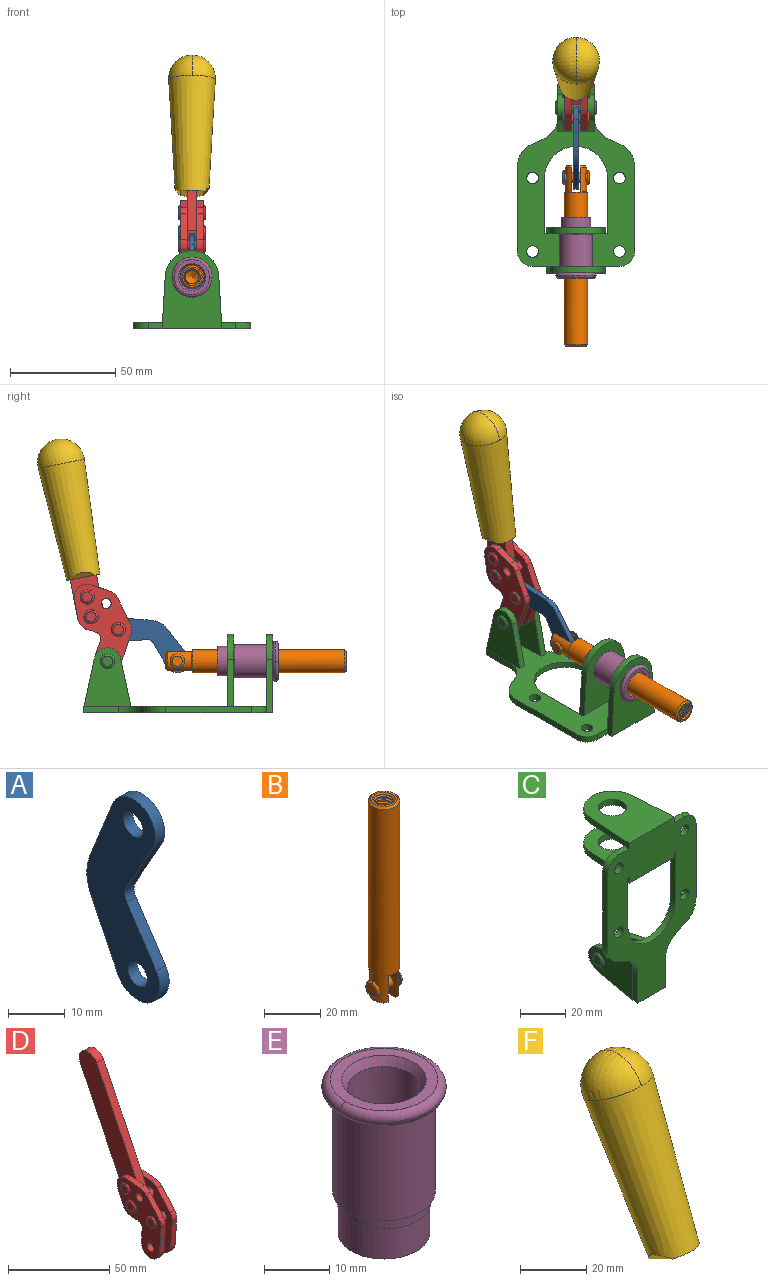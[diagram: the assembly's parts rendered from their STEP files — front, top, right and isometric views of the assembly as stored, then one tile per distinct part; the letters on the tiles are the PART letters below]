
ASSEMBLY  parts=6 mates=6
PART A: 12 faces, bbox 2.3x18.2x42.8 mm
  f0: cylinder r=2.4mm len=4.8mm, axis (1,0,0), area 34.9mm2, adj f4,f11
  f1: cylinder r=10.41mm len=8.47mm, axis (1,0,0), area 20.2mm2, adj f4,f9,f10,f11
  f2: cylinder r=3.05mm len=3.16mm, axis (1,0,0), area 7.7mm2, adj f4,f6,f7,f11
  f3: cylinder r=2.4mm len=4.8mm, axis (1,0,0), area 34.9mm2, adj f4,f11
  f4: plane 42.81x18.23mm, normal (-1,0,0), area 414.1mm2, adj f0,f1,f2,f3,f5,f6,f7,f8
  f5: cylinder r=5.54mm len=10.67mm, axis (1,0,0), area 41.8mm2, adj f4,f6,f10,f11
  f6: plane 11.66x6.53mm, normal (0,-0.87,-0.49), area 30.9mm2, adj f2,f4,f5,f11
  f7: plane 11.17x7.33mm, normal (0,-0.84,0.55), area 30.9mm2, adj f2,f4,f8,f11
  f8: cylinder r=5.54mm len=10.51mm, axis (1,0,0), area 41.8mm2, adj f4,f7,f9,f11
  f9: plane 13.67x6.67mm, normal (0,0.9,-0.44), area 35.1mm2, adj f1,f4,f8,f11
  f10: plane 14.1x5.7mm, normal (0,0.93,0.37), area 35.1mm2, adj f1,f4,f5,f11
  f11: plane 42.81x18.23mm, normal (1,0,0), area 414.1mm2, adj f0,f1,f2,f3,f5,f6,f7,f8
PART B: 48 faces, bbox 12.6x11.1x86.1 mm
  f0: torus R=2.41mm, axis (-1,0,0), area 15mm2, adj f30,f32,f34
  f1: torus R=2.41mm, axis (-1,0,0), area 15mm2, adj f29,f31,f33
  f2: cylinder r=5.54mm len=72.39mm, axis (0,0,1), area 2518.5mm2, adj f3,f4,f42,f43
  f3: cone r=5.54mm half-angle=45deg, axis (0,0,1), area 7.6mm2, adj f2,f5,f41
  f4: cone r=5.54mm half-angle=45deg, axis (0,0,-1), area 34.9mm2, adj f2,f39
  f5: cylinder r=5.08mm len=11.48mm, axis (0,0,1), area 108.3mm2, adj f3,f7,f8,f41
  f6: cylinder r=2.41mm len=4.83mm, axis (-1,0,0), area 71.2mm2, adj f40,f41
  f7: cylinder r=2.41mm len=4.83mm, axis (-1,0,0), area 7.6mm2, adj f5,f34
  f8: cone r=5.08mm half-angle=45deg, axis (0,0,1), area 10.6mm2, adj f5,f37,f41
  f9: cone r=3.98mm half-angle=45deg, axis (0,0,1), area 17.6mm2, adj f27,f39,f45,f46,f47
  f10: cylinder r=2.41mm len=4.83mm, axis (-1,0,0), area 7.6mm2, adj f33,f38
  f11: cylinder r=3.2mm len=6.4mm, axis (0,0,1), area 78.4mm2, adj f12,f28,f44,f45,f47
  f12: cylinder r=3.2mm len=6.4mm, axis (0,0,1), area 10.5mm2, adj f11,f13,f45,f47
  f13: cylinder r=3.2mm len=6.4mm, axis (0,0,1), area 10.5mm2, adj f12,f14,f45,f47
  f14: cylinder r=3.2mm len=6.4mm, axis (0,0,1), area 10.5mm2, adj f13,f15,f45,f47
  f15: cylinder r=3.2mm len=6.4mm, axis (0,0,1), area 10.5mm2, adj f14,f16,f45,f47
  f16: cylinder r=3.2mm len=6.4mm, axis (0,0,1), area 10.5mm2, adj f15,f17,f45,f47
  f17: cylinder r=3.2mm len=6.4mm, axis (0,0,1), area 10.5mm2, adj f16,f18,f45,f47
  f18: cylinder r=3.2mm len=6.4mm, axis (0,0,1), area 10.5mm2, adj f17,f19,f45,f47
  f19: cylinder r=3.2mm len=6.4mm, axis (0,0,1), area 10.5mm2, adj f18,f20,f45,f47
  f20: cylinder r=3.2mm len=6.4mm, axis (0,0,1), area 10.5mm2, adj f19,f21,f45,f47
  f21: cylinder r=3.2mm len=6.4mm, axis (0,0,1), area 10.5mm2, adj f20,f22,f45,f47
  f22: cylinder r=3.2mm len=6.4mm, axis (0,0,1), area 10.5mm2, adj f21,f23,f45,f47
  f23: cylinder r=3.2mm len=6.4mm, axis (0,0,1), area 10.5mm2, adj f22,f24,f45,f47
  f24: cylinder r=3.2mm len=6.4mm, axis (0,0,1), area 10.5mm2, adj f23,f25,f45,f47
  f25: cylinder r=3.2mm len=6.4mm, axis (0,0,1), area 10.5mm2, adj f24,f26,f45,f47
  f26: cylinder r=3.2mm len=6.4mm, axis (0,0,1), area 10.5mm2, adj f25,f27,f45,f47
  f27: cylinder r=3.2mm len=6.4mm, axis (0,0,1), area 7.4mm2, adj f9,f26,f45,f47
  f28: cone r=3.2mm half-angle=60deg, axis (0,0,1), area 37.2mm2, adj f11
  f29: plane 4.83x4.83mm, normal (-1,0,0), area 18.3mm2, adj f1,f31
  f30: plane 4.83x4.83mm, normal (1,0,0), area 18.3mm2, adj f0,f32
  f31: torus R=2.41mm, axis (-1,0,0), area 15mm2, adj f1,f29,f33
  f32: torus R=2.41mm, axis (-1,0,0), area 15mm2, adj f0,f30,f34
  f33: plane 6.83x6.83mm, normal (1,0,0), area 18.3mm2, adj f1,f10,f31
  f34: plane 6.83x6.83mm, normal (-1,0,0), area 18.3mm2, adj f0,f7,f32
  f35: cone r=5.08mm half-angle=45deg, axis (0,0,1), area 10.6mm2, adj f36,f38,f40
  f36: plane 7.25x1.97mm, normal (0,0,-1), area 10mm2, adj f35,f40
  f37: plane 7.25x1.97mm, normal (0,0,-1), area 10mm2, adj f8,f41
  f38: cylinder r=5.08mm len=11.48mm, axis (0,0,1), area 108.3mm2, adj f10,f35,f40,f42
  f39: plane 9.55x9.55mm, normal (0,0,1), area 22mm2, adj f4,f9
  f40: plane 12.76x10.09mm, normal (1,0,0), area 95.7mm2, adj f6,f35,f36,f38,f42,f43
  f41: plane 12.76x10.09mm, normal (-1,0,0), area 95.7mm2, adj f3,f5,f6,f8,f37,f43
  f42: cone r=5.54mm half-angle=45deg, axis (0,0,1), area 7.6mm2, adj f2,f38,f40
  f43: plane 11.07x4.7mm, normal (0,0,-1), area 50.4mm2, adj f2,f40,f41
  f44: plane 0.89x0.62mm, normal (-1,0,0), area 0.3mm2, adj f11,f45,f46,f47
  f45: bspline ~24.8x7.63mm, area 266.6mm2, adj f9,f11,f12,f13,f14,f15,f16,f17
  f46: bspline ~24.87x7.63mm, area 73.6mm2, adj f9,f44,f45,f47
  f47: bspline ~24.98x7.63mm, area 272.5mm2, adj f9,f11,f12,f13,f14,f15,f16,f17
PART C: 55 faces, bbox 55.7x37.4x89.8 mm
  f0: torus R=2.41mm, axis (-1,0,0), area 15mm2, adj f11,f15,f25
  f1: torus R=2.41mm, axis (-1,0,0), area 15mm2, adj f10,f12,f22
  f2: cylinder r=2.78mm len=5.56mm, axis (0,-1,0), area 54.2mm2, adj f30,f54
  f3: cylinder r=14.99mm len=29.97mm, axis (0,-1,0), area 145.9mm2, adj f30,f49,f53,f54
  f4: cylinder r=2.78mm len=5.56mm, axis (0,-1,0), area 54.2mm2, adj f30,f54
  f5: cylinder r=2.78mm len=5.56mm, axis (0,-1,0), area 54.2mm2, adj f30,f54
  f6: cylinder r=2.78mm len=5.56mm, axis (0,-1,0), area 54.2mm2, adj f30,f54
  f7: cylinder r=6.35mm len=12.7mm, axis (0,0,1), area 123.6mm2, adj f27,f51
  f8: cylinder r=6.35mm len=12.7mm, axis (0,0,-1), area 124.7mm2, adj f21,f35
  f9: cylinder r=2.41mm len=11.18mm, axis (-1,0,0), area 169.4mm2, adj f16,f19
  f10: plane 4.83x4.83mm, normal (1,0,0), area 18.3mm2, adj f1,f12
  f11: plane 4.83x4.83mm, normal (-1,0,0), area 18.3mm2, adj f0,f15
  f12: torus R=2.41mm, axis (-1,0,0), area 15mm2, adj f1,f10,f22
  f13: cylinder r=6.35mm len=12.41mm, axis (1,0,0), area 53.4mm2, adj f18,f19,f22,f23
  f14: cylinder r=6.35mm len=12.41mm, axis (-1,0,0), area 53.4mm2, adj f16,f17,f24,f25
  f15: torus R=2.41mm, axis (-1,0,0), area 15mm2, adj f0,f11,f25
  f16: plane 27.86x22.35mm, normal (1,0,0), area 425.4mm2, adj f9,f14,f17,f24,f30
  f17: plane 22.86x4.97mm, normal (0,0.21,0.98), area 72.5mm2, adj f14,f16,f25,f30
  f18: plane 22.86x4.97mm, normal (0,0.21,0.98), area 72.5mm2, adj f13,f19,f22,f30
  f19: plane 27.86x22.35mm, normal (-1,0,0), area 425.4mm2, adj f9,f13,f18,f23,f30
  f20: cylinder r=12.7mm len=25.35mm, axis (0,0,-1), area 119.8mm2, adj f21,f34,f35,f36
  f21: plane 34.21x28.07mm, normal (0,0,-1), area 702.4mm2, adj f8,f20,f30,f34,f36
  f22: plane 27.96x22.45mm, normal (1,0,0), area 407.2mm2, adj f1,f12,f13,f18,f23,f30,f42,f43
  f23: plane 22.86x4.97mm, normal (0,0.21,-0.98), area 72.5mm2, adj f13,f19,f22,f44
  f24: plane 22.86x4.97mm, normal (0,0.21,-0.98), area 72.5mm2, adj f14,f16,f25,f44
  f25: plane 27.86x22.35mm, normal (-1,0,0), area 407.1mm2, adj f0,f14,f15,f17,f24,f30,f45,f46
  f26: plane 3.1x0.95mm, normal (0,0,-1), area 2.7mm2, adj f30,f49,f50,f54
  f27: plane 34.21x28.07mm, normal (0,0,1), area 702.4mm2, adj f7,f28,f30,f50,f52
  f28: cylinder r=12.7mm len=25.35mm, axis (0,0,1), area 118.8mm2, adj f27,f50,f51,f52
  f29: plane 3.1x0.95mm, normal (0,0,-1), area 2.7mm2, adj f30,f52,f53,f54
  f30: plane 86.54x55.63mm, normal (0,1,0), area 2362.9mm2, adj f2,f3,f4,f5,f6,f16,f17,f18
  f31: plane 40.56x3.1mm, normal (-1,0,0), area 125.7mm2, adj f30,f32,f48,f54
  f32: cylinder r=7.11mm len=7.11mm, axis (0,-1,0), area 34.6mm2, adj f30,f31,f33,f54
  f33: plane 6.67x3.1mm, normal (0,0,1), area 20.4mm2, adj f30,f32,f34,f54
  f34: plane 25.39x3.13mm, normal (-1,0.06,0), area 79.5mm2, adj f20,f21,f33,f35,f54
  f35: plane 37.31x28.45mm, normal (0,0,1), area 789.9mm2, adj f8,f20,f34,f36,f54
  f36: plane 25.39x3.13mm, normal (1,0.06,0), area 79.5mm2, adj f20,f21,f35,f37,f54
  f37: plane 6.67x3.1mm, normal (0,0,1), area 20.4mm2, adj f30,f36,f38,f54
  f38: cylinder r=7.11mm len=7.11mm, axis (0,-1,0), area 34.6mm2, adj f30,f37,f39,f54
  f39: plane 40.56x3.1mm, normal (1,0,0), area 125.7mm2, adj f30,f38,f40,f54
  f40: cylinder r=11.18mm len=10.16mm, axis (0,-1,0), area 39.5mm2, adj f30,f39,f41,f54
  f41: plane 6.09x3.1mm, normal (0.42,0,-0.91), area 20.8mm2, adj f30,f40,f42,f54
  f42: cylinder r=11.18mm len=9.41mm, axis (0,-1,0), area 37.2mm2, adj f22,f30,f41,f43,f54
  f43: plane 16.5x3.1mm, normal (1,0,0), area 51.1mm2, adj f22,f42,f44,f54
  f44: plane 17.37x3.1mm, normal (0,0,-1), area 53.8mm2, adj f23,f24,f30,f43,f45,f54
  f45: plane 16.5x3.1mm, normal (-1,0,0), area 51.1mm2, adj f25,f44,f46,f54
  f46: cylinder r=11.18mm len=9.41mm, axis (0,-1,0), area 37.2mm2, adj f25,f30,f45,f47,f54
  f47: plane 6.09x3.1mm, normal (-0.42,0,-0.91), area 20.8mm2, adj f30,f46,f48,f54
  f48: cylinder r=11.18mm len=10.16mm, axis (0,-1,0), area 39.5mm2, adj f30,f31,f47,f54
  f49: plane 26.54x3.1mm, normal (-1,0,0), area 82.3mm2, adj f3,f26,f30,f54
  f50: plane 25.39x3.1mm, normal (1,0.06,0), area 78.8mm2, adj f26,f27,f28,f51,f54
  f51: plane 37.31x28.45mm, normal (0,0,-1), area 789.9mm2, adj f7,f28,f50,f52,f54
  f52: plane 25.39x3.1mm, normal (-1,0.06,0), area 78.8mm2, adj f27,f28,f29,f51,f54
  f53: plane 26.54x3.1mm, normal (1,0,0), area 82.3mm2, adj f3,f29,f30,f54
  f54: plane 89.66x55.63mm, normal (0,-1,0), area 2678.5mm2, adj f2,f3,f4,f5,f6,f26,f29,f31
PART D: 59 faces, bbox 12.9x60.2x99.6 mm
  f0: torus R=2.39mm, axis (-1,0,0), area 14.9mm2, adj f20,f43,f51
  f1: torus R=2.39mm, axis (-1,0,0), area 14.9mm2, adj f19,f42,f51
  f2: torus R=2.39mm, axis (-1,0,0), area 14.9mm2, adj f18,f35,f51
  f3: torus R=2.39mm, axis (-1,0,0), area 14.9mm2, adj f14,f17,f23
  f4: torus R=2.39mm, axis (-1,0,0), area 14.9mm2, adj f13,f16,f23
  f5: torus R=2.39mm, axis (-1,0,0), area 14.9mm2, adj f12,f15,f23
  f6: cylinder r=2.39mm len=4.78mm, axis (1,0,0), area 46.5mm2, adj f48,f50,f51
  f7: cylinder r=2.39mm len=4.78mm, axis (1,0,0), area 46.5mm2, adj f50,f51
  f8: cylinder r=6.35mm len=12.68mm, axis (1,0,0), area 61.8mm2, adj f38,f39,f50,f51
  f9: cylinder r=2.39mm len=4.78mm, axis (-1,0,0), area 70.5mm2, adj f46,f50
  f10: cylinder r=2.39mm len=4.78mm, axis (-1,0,0), area 46.5mm2, adj f23,f45,f46
  f11: cylinder r=2.39mm len=4.78mm, axis (-1,0,0), area 46.5mm2, adj f23,f46
  f12: plane 4.78x4.78mm, normal (1,0,0), area 17.9mm2, adj f5,f15
  f13: plane 4.78x4.78mm, normal (1,0,0), area 17.9mm2, adj f4,f16
  f14: plane 4.78x4.78mm, normal (1,0,0), area 17.9mm2, adj f3,f17
  f15: torus R=2.39mm, axis (-1,0,0), area 14.9mm2, adj f5,f12,f23
  f16: torus R=2.39mm, axis (-1,0,0), area 14.9mm2, adj f4,f13,f23
  f17: torus R=2.39mm, axis (-1,0,0), area 14.9mm2, adj f3,f14,f23
  f18: plane 4.78x4.78mm, normal (-1,0,0), area 17.9mm2, adj f2,f35
  f19: plane 4.78x4.78mm, normal (-1,0,0), area 17.9mm2, adj f1,f42
  f20: plane 4.78x4.78mm, normal (-1,0,0), area 17.9mm2, adj f0,f43
  f21: plane 2.26x0.2mm, normal (1,0,0), area 0.2mm2, adj f31,f44
  f22: plane 2.26x0.2mm, normal (-1,0,0), area 0.2mm2, adj f41,f44
  f23: plane 39.37x30.77mm, normal (1,0,0), area 565.5mm2, adj f3,f4,f5,f10,f11,f15,f16,f17
  f24: cylinder r=6.1mm len=4.15mm, axis (-1,0,0), area 14.7mm2, adj f23,f25,f32,f46
  f25: plane 10.25x9.01mm, normal (0,-0.75,0.66), area 42.3mm2, adj f23,f24,f26,f46
  f26: cylinder r=6.35mm len=4.64mm, axis (-1,0,0), area 15.6mm2, adj f23,f25,f27,f46
  f27: plane 15.84x3.1mm, normal (0,-1,-0.07), area 49.2mm2, adj f23,f26,f28,f46
  f28: cylinder r=6.35mm len=12.68mm, axis (-1,0,0), area 61.8mm2, adj f23,f27,f29,f46
  f29: plane 8.11x3.1mm, normal (0,1,0.07), area 25.2mm2, adj f23,f28,f30,f46
  f30: cylinder r=3.05mm len=3.25mm, axis (-1,0,0), area 14.8mm2, adj f23,f29,f31,f46
  f31: plane 5.99x3.1mm, normal (0,0.07,-1), area 18.6mm2, adj f21,f23,f30,f44,f46
  f32: plane 9.5x3.1mm, normal (0,-0.07,1), area 29.5mm2, adj f23,f24,f33,f46,f47
  f33: cylinder r=6.1mm len=8.63mm, axis (-1,0,0), area 39.1mm2, adj f23,f32,f34,f47
  f34: plane 8.65x3.96mm, normal (0,0.91,-0.42), area 29.5mm2, adj f23,f33,f44,f47
  f35: torus R=2.39mm, axis (-1,0,0), area 14.9mm2, adj f2,f18,f51
  f36: plane 10.25x9.01mm, normal (0,-0.75,0.66), area 42.3mm2, adj f37,f49,f50,f51
  f37: cylinder r=6.35mm len=4.64mm, axis (1,0,0), area 15.6mm2, adj f36,f38,f50,f51
  f38: plane 15.84x3.1mm, normal (0,-1,-0.07), area 49.2mm2, adj f8,f37,f50,f51
  f39: plane 8.11x3.1mm, normal (0,1,0.07), area 25.2mm2, adj f8,f40,f50,f51
  f40: cylinder r=3.05mm len=3.25mm, axis (1,0,0), area 14.8mm2, adj f39,f41,f50,f51
  f41: plane 5.99x3.1mm, normal (0,0.07,-1), area 18.6mm2, adj f22,f40,f44,f50,f51
  f42: torus R=2.39mm, axis (-1,0,0), area 14.9mm2, adj f1,f19,f51
  f43: torus R=2.39mm, axis (-1,0,0), area 14.9mm2, adj f0,f20,f51
  f44: cylinder r=6.35mm len=12.12mm, axis (-1,0,0), area 128.9mm2, adj f21,f22,f23,f31,f34,f41,f46,f47
  f45: plane 2.65x1.35mm, normal (1,0,0), area 1mm2, adj f10,f55
  f46: plane 39.08x20.42mm, normal (-1,0,0), area 412.5mm2, adj f9,f10,f11,f24,f25,f26,f27,f28
  f47: plane 77.62x39.82mm, normal (1,0,0), area 850mm2, adj f32,f33,f34,f44,f53,f54,f55
  f48: plane 2.65x1.35mm, normal (-1,0,0), area 1mm2, adj f6,f55
  f49: cylinder r=6.1mm len=4.15mm, axis (1,0,0), area 14.7mm2, adj f36,f50,f51,f56
  f50: plane 39.08x20.42mm, normal (1,0,0), area 412.5mm2, adj f6,f7,f8,f9,f36,f37,f38,f39
  f51: plane 39.37x30.77mm, normal (-1,0,0), area 565.5mm2, adj f0,f1,f2,f6,f7,f8,f35,f36
  f52: plane 8.65x3.96mm, normal (0,0.91,-0.42), area 29.5mm2, adj f44,f51,f57,f58
  f53: plane 68.49x33.4mm, normal (0,0.9,-0.44), area 358.1mm2, adj f44,f47,f54,f58
  f54: cylinder r=6.35mm len=12.06mm, axis (1,0,0), area 93.7mm2, adj f47,f53,f55,f58
  f55: plane 68.49x33.4mm, normal (0,-0.9,0.44), area 358.1mm2, adj f44,f45,f46,f47,f48,f50,f54,f58
  f56: plane 9.5x3.1mm, normal (0,-0.07,1), area 29.5mm2, adj f49,f50,f51,f57,f58
  f57: cylinder r=6.1mm len=8.63mm, axis (1,0,0), area 39.1mm2, adj f51,f52,f56,f58
  f58: plane 77.62x39.82mm, normal (-1,0,0), area 850mm2, adj f44,f52,f53,f54,f55,f56,f57
PART E: 15 faces, bbox 20.6x20.6x28.7 mm
  f0: torus R=8.26mm, axis (0,0,1), area 56.8mm2, adj f1,f10,f12
  f1: torus R=8.26mm, axis (0,0,1), area 56.8mm2, adj f0,f6,f13
  f2: cylinder r=5.59mm len=25.91mm, axis (0,0,1), area 909.6mm2, adj f3,f4
  f3: cone r=6.86mm half-angle=45deg, axis (0,0,-1), area 70.2mm2, adj f2,f14
  f4: cone r=6.47mm half-angle=30deg, axis (0,0,1), area 66.7mm2, adj f2,f13
  f5: cylinder r=7.04mm len=14.07mm, axis (0,0,1), area 252.6mm2, adj f11,f14
  f6: torus R=8.26mm, axis (0,0,1), area 56.8mm2, adj f1,f12,f13
  f7: cylinder r=7.16mm len=14.33mm, axis (0,0,1), area 91.5mm2, adj f9,f11
  f8: cylinder r=7.86mm len=18.42mm, axis (0,0,1), area 909.6mm2, adj f9,f10
  f9: plane 15.72x15.72mm, normal (0,0,-1), area 33mm2, adj f7,f8
  f10: plane 16.51x16.51mm, normal (0,0,-1), area 19.9mm2, adj f0,f8,f12
  f11: plane 14.33x14.33mm, normal (0,0,-1), area 5.7mm2, adj f5,f7
  f12: torus R=8.26mm, axis (0,0,1), area 56.8mm2, adj f0,f6,f10
  f13: plane 16.51x16.51mm, normal (0,0,1), area 82.7mm2, adj f1,f4,f6
  f14: plane 14.07x14.07mm, normal (0,0,-1), area 7.8mm2, adj f3,f5
PART F: 11 faces, bbox 22.3x42.6x64.5 mm
  f0: sphere r=11.13mm, area 411.4mm2, adj f1,f8
  f1: cone r=11.11mm half-angle=3.3deg, axis (0,0.44,0.9), area 3251.8mm2, adj f0,f7,f8,f9,f10
  f2: cylinder r=6.16mm len=11.7mm, axis (1,0,0), area 89.5mm2, adj f3,f4,f5,f6
  f3: plane 60.23x36.75mm, normal (-1,0,0), area 763.6mm2, adj f2,f4,f6,f10
  f4: plane 51.37x25.05mm, normal (0,0.9,-0.44), area 264.2mm2, adj f2,f3,f5,f10
  f5: plane 60.23x36.75mm, normal (1,0,0), area 763.6mm2, adj f2,f4,f6,f10
  f6: plane 51.37x25.05mm, normal (0,-0.9,0.44), area 264.2mm2, adj f2,f3,f5,f10
  f7: plane 9.95x5.95mm, normal (0.71,-0.31,-0.64), area 25.8mm2, adj f1,f10
  f8: sphere r=11.13mm, area 411.4mm2, adj f0,f1
  f9: plane 9.95x5.95mm, normal (-0.71,-0.31,-0.64), area 25.8mm2, adj f1,f10
  f10: plane 14.27x11.38mm, normal (0,-0.44,-0.9), area 106.7mm2, adj f1,f3,f4,f5,f6,f7,f9
PLACE A rot(axis=(0,-0.53,-0.85),180deg) t=(0,33.05,10.71)mm
PLACE B rot(axis=(1,0,0),90deg) t=(0,23.56,0)mm
PLACE C rot(axis=(1,0,0),90deg) t=(0,9.14,0)mm fixed
PLACE D rot(axis=(1,0,0),15deg) t=(0,9.15,49.24)mm
PLACE E rot(axis=(1,0,0),90deg) t=(0,9.14,0)mm
PLACE F rot(axis=(1,0,0),15deg) t=(0,9.15,49.24)mm
MATE fastened F.f2 <-> D.f54  axis (1,0,0) through (0,63.6,120.54)mm
MATE revolute D.f4 <-> A.f5  axis (-1,0,0) through (0,36.06,39.62)mm
MATE slider B.f2 <-> E.f2  axis (0,-1,0) through (0,-35.22,24.61)mm
MATE revolute A.f3 <-> B.f6  axis (-1,0,0) through (0,8.09,24.61)mm
MATE revolute D.f7 <-> C.f0  axis (1,0,0) through (0,41.23,24.61)mm
MATE fastened E.f2 <-> C.f7  axis (0,1,0) through (0,-37.25,24.61)mm
